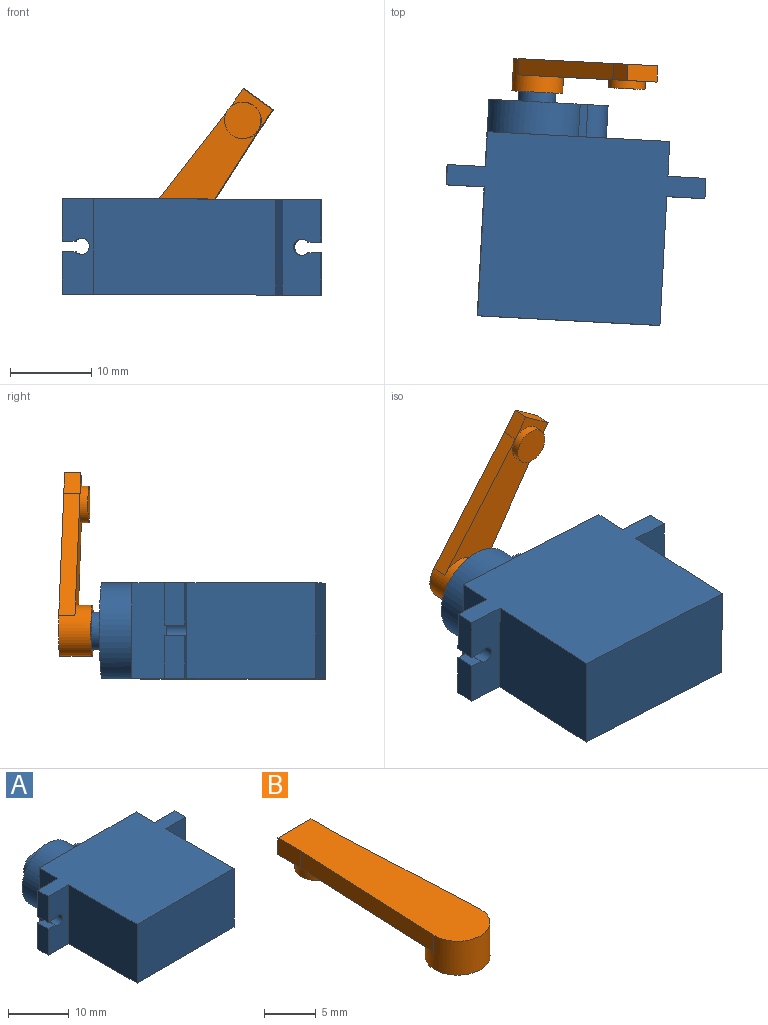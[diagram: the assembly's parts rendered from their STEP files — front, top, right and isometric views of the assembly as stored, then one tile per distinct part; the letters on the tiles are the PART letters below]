
ASSEMBLY  parts=2 mates=1
PART A: 33 faces, bbox 31.9x29.9x11.8 mm
  f0: plane 31.9x22.7mm, normal (0,0,1), area 534.2mm2, adj f1,f2,f3,f4,f6,f21,f22,f23
  f1: plane 22.5x11.8mm, normal (0,-1,0), area 265.5mm2, adj f0,f5,f29,f31
  f2: plane 16.6x11.8mm, normal (0,1,0), area 128.5mm2, adj f0,f5,f6,f8,f9,f10,f11
  f3: plane 5.9x5.9mm, normal (0,1,0), area 7.5mm2, adj f0,f4,f9
  f4: plane 11.8x4.3mm, normal (-1,0,0), area 50.7mm2, adj f0,f3,f5,f7,f28
  f5: plane 31.9x22.7mm, normal (0,0,-1), area 534.2mm2, adj f1,f2,f4,f6,f7,f17,f22,f27
  f6: plane 11.8x4.3mm, normal (1,0,0), area 50.7mm2, adj f0,f2,f5,f22
  f7: plane 5.9x5.9mm, normal (0,1,0), area 7.5mm2, adj f4,f5,f9
  f8: plane 4x0.96mm, normal (0,0,1), area 3.8mm2, adj f2,f9,f11,f12
  f9: cylinder r=5.9mm len=11.8mm, axis (0,-1,0), area 127.6mm2, adj f2,f3,f7,f8,f10,f12
  f10: plane 4x0.96mm, normal (0,0,-1), area 3.8mm2, adj f2,f9,f11,f12
  f11: cylinder r=2.5mm len=5mm, axis (0,-1,0), area 31.4mm2, adj f2,f8,f10,f12
  f12: plane 14.7x11.8mm, normal (0,1,0), area 105.5mm2, adj f8,f9,f10,f11,f13
  f13: cylinder r=2.3mm len=4.6mm, axis (0,-1,0), area 46.2mm2, adj f12,f15
  f14: cylinder r=0.85mm len=3.2mm, axis (0,-1,0), area 17.1mm2, adj f15,f16
  f15: plane 4.6x4.6mm, normal (0,1,0), area 14.3mm2, adj f13,f14
  f16: plane 1.7x1.7mm, normal (0,1,0), area 2.3mm2, adj f14
  f17: plane 5.25x2.5mm, normal (1,0,0), area 13.1mm2, adj f5,f18,f22,f32
  f18: plane 2.5x1.59mm, normal (0,0,1), area 4mm2, adj f17,f19,f22,f32
  f19: cylinder r=1mm len=2.5mm, axis (0,-1,0), area 12.2mm2, adj f18,f20,f22,f32
  f20: plane 2.5x1.59mm, normal (0,0,-1), area 4mm2, adj f19,f21,f22,f32
  f21: plane 5.25x2.5mm, normal (1,0,0), area 13.1mm2, adj f0,f20,f22,f32
  f22: plane 11.8x4.7mm, normal (0,1,0), area 50.5mm2, adj f0,f5,f6,f17,f18,f19,f20,f21
  f23: plane 5.25x2.5mm, normal (-1,0,0), area 13.1mm2, adj f0,f24,f28,f30
  f24: plane 2.5x1.59mm, normal (0,0,-1), area 4mm2, adj f23,f25,f28,f30
  f25: cylinder r=1mm len=2.5mm, axis (0,-1,0), area 12.2mm2, adj f24,f26,f28,f30
  f26: plane 2.5x1.59mm, normal (0,0,1), area 4mm2, adj f25,f27,f28,f30
  f27: plane 5.25x2.5mm, normal (-1,0,0), area 13.1mm2, adj f5,f26,f28,f30
  f28: plane 11.8x4.7mm, normal (0,1,0), area 50.5mm2, adj f0,f4,f5,f23,f24,f25,f26,f27
  f29: plane 15.9x11.8mm, normal (-1,0,0), area 187.6mm2, adj f0,f1,f5,f30
  f30: plane 11.8x4.7mm, normal (0,-1,0), area 50.5mm2, adj f0,f5,f23,f24,f25,f26,f27,f29
  f31: plane 15.9x11.8mm, normal (1,0,0), area 187.6mm2, adj f0,f1,f5,f32
  f32: plane 11.8x4.7mm, normal (0,-1,0), area 50.5mm2, adj f0,f5,f17,f18,f19,f20,f21,f31
PART B: 14 faces, bbox 6.2x25.4x4 mm
  f0: cylinder r=2.35mm len=4.7mm, axis (0,0,1), area 29.5mm2, adj f2,f4
  f1: cylinder r=3.12mm len=6.25mm, axis (0,0,1), area 59.5mm2, adj f2,f3,f5,f6,f7
  f2: plane 6.25x6.25mm, normal (0,0,-1), area 13.3mm2, adj f0,f1
  f3: plane 25.35x6.25mm, normal (0,0,1), area 132.1mm2, adj f1,f5,f6,f10,f11,f12
  f4: plane 4.7x4.7mm, normal (0,0,-1), area 17.3mm2, adj f0
  f5: plane 19.01x2mm, normal (1,0.05,0), area 38.1mm2, adj f1,f3,f7,f10
  f6: plane 19.01x2mm, normal (-1,0.05,0), area 38.1mm2, adj f1,f3,f7,f12
  f7: plane 19.01x6.24mm, normal (0,0,-1), area 79.2mm2, adj f1,f5,f6,f8
  f8: cylinder r=2.25mm len=4.5mm, axis (0,0,1), area 14.1mm2, adj f7,f9,f13
  f9: plane 4.5x4.5mm, normal (0,0,-1), area 15.9mm2, adj f8
  f10: plane 3.07x2mm, normal (1,0,0), area 6.1mm2, adj f3,f5,f11,f13
  f11: plane 4.5x2mm, normal (0,1,0), area 9mm2, adj f3,f10,f12,f13
  f12: plane 3.07x2mm, normal (-1,0,0), area 6.1mm2, adj f3,f6,f11,f13
  f13: plane 4.5x3.07mm, normal (0,0,-1), area 6.3mm2, adj f8,f10,f11,f12
PLACE A rot(axis=(0,0.07,-1),3.1deg) t=(-1.61,-0.65,-0.05)mm
PLACE B rot(axis=(-0.24,-0.68,-0.69),157.4deg) t=(-12.91,31.9,0)mm
MATE revolute A.f9 <-> B.f0  axis (0.05,1,0) through (-13.01,29.9,0)mm
